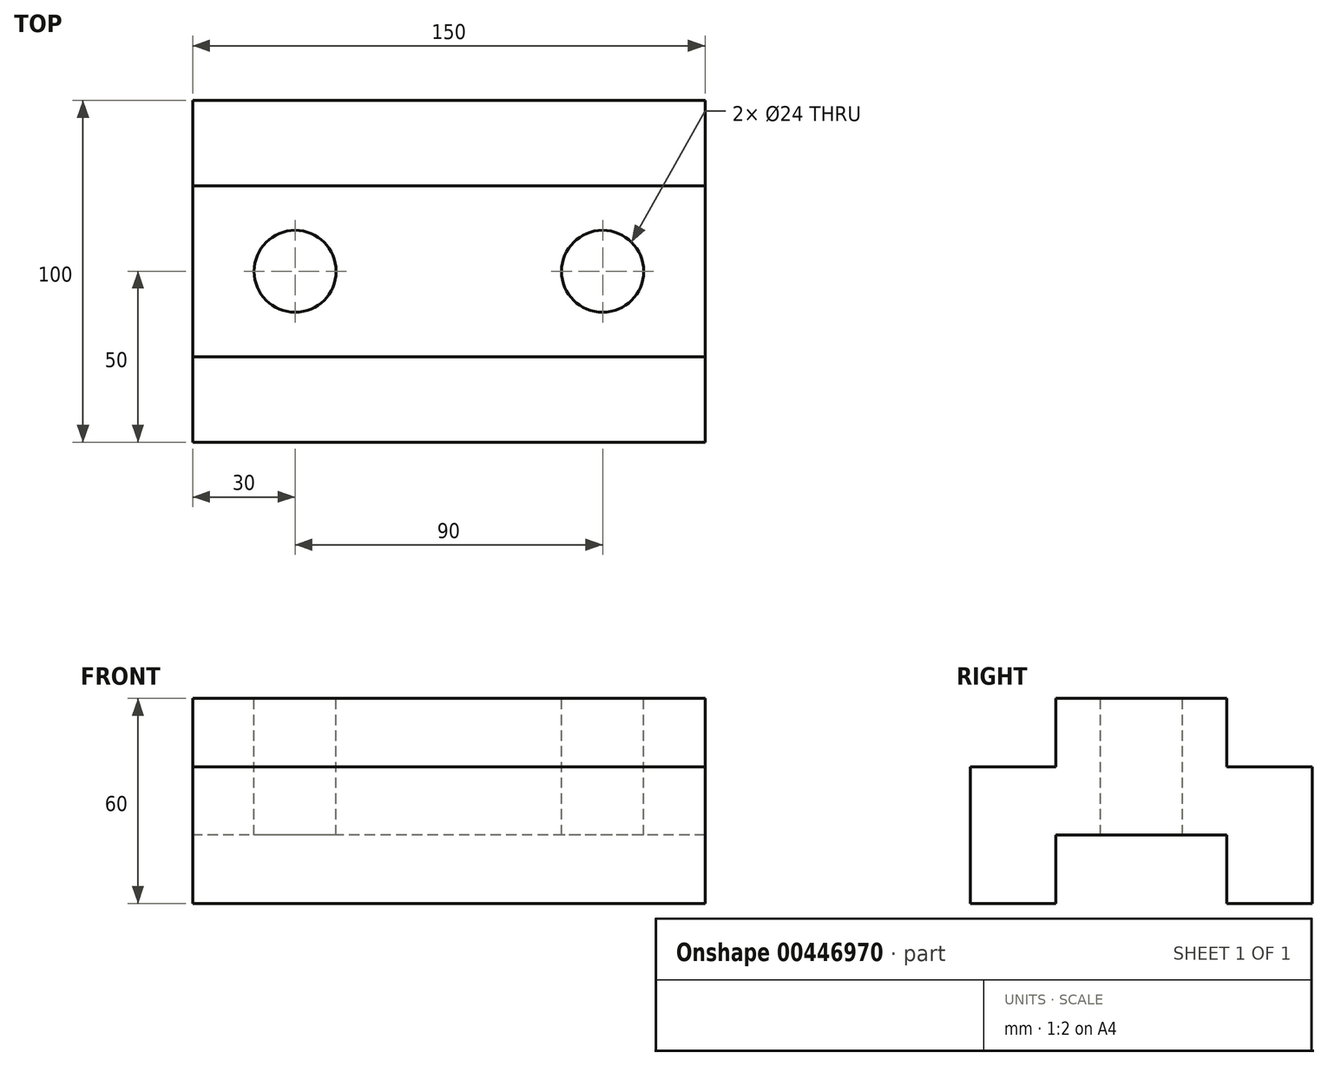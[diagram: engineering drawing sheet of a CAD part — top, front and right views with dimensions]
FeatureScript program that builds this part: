
annotation { "Feature Type Name" : "Feature", "Feature Type Description" : "" }
export const myFeature = defineFeature(function(context is Context, id is Id, definition is map)
    precondition{}
    {
        {
            var Q0;
            Q0=qCreatedBy(makeId("Right.planeOp"),FACE);
            var sketch = newSketch(context, id + "F0", { "sketchPlane" : qUnion([Q0])});
            skLineSegment(sketch, "E0", {"start": v(0, 0) * mm, "end": v(0, 73.04) * mm, "construction": true});
            skLineSegment(sketch, "E1", {"start": v(0, 60) * mm, "end": v(25, 60) * mm});
            skLineSegment(sketch, "E2", {"start": v(25, 60) * mm, "end": v(25, 40) * mm});
            skLineSegment(sketch, "E3", {"start": v(25, 40) * mm, "end": v(50, 40) * mm});
            skLineSegment(sketch, "E4", {"start": v(50, 40) * mm, "end": v(50, 0) * mm});
            skLineSegment(sketch, "E5", {"start": v(50, 0) * mm, "end": v(25, 0) * mm});
            skLineSegment(sketch, "E6", {"start": v(25, 0) * mm, "end": v(25, 20) * mm});
            skLineSegment(sketch, "E7", {"start": v(25, 20) * mm, "end": v(0, 20) * mm});
            skLineSegment(sketch, "E8.MirrorCS", {"start": v(0, 60) * mm, "end": v(-25, 60) * mm});
            skLineSegment(sketch, "E9.MirrorCS", {"start": v(-25, 60) * mm, "end": v(-25, 40) * mm});
            skLineSegment(sketch, "E10.MirrorCS", {"start": v(-25, 40) * mm, "end": v(-50, 40) * mm});
            skLineSegment(sketch, "E11.MirrorCS", {"start": v(-50, 40) * mm, "end": v(-50, 0) * mm});
            skLineSegment(sketch, "E12.MirrorCS", {"start": v(-50, 0) * mm, "end": v(-25, 0) * mm});
            skLineSegment(sketch, "E13.MirrorCS", {"start": v(-25, 0) * mm, "end": v(-25, 20) * mm});
            skLineSegment(sketch, "E14.MirrorCS", {"start": v(-25, 20) * mm, "end": v(0, 20) * mm});
            skSolve(sketch);
        }
        {
            var Q0;
            Q0 = qSketchRegion(id + "F0", true);
            extrude(context, id + "F1", {"entities" : qUnion([Q0]), "endBound" : BoundingType.SYMMETRIC, "depth" : 150 * mm});
        }
        {
            var Q0;
            Q0=makeQuery(id+"F1.opExtrude","SWEPT_FACE",FACE,{"disambiguationData":[OSD([sQuery(id+"F0.wireOp",EDGE,"E1"),sQuery(id+"F0.wireOp",EDGE,"E8.MirrorCS")])]});
            var sketch = newSketch(context, id + "F2", { "sketchPlane" : qUnion([Q0])});
            skLineSegment(sketch, "E15", {"start": v(-75, 0) * mm, "end": v(75, 0) * mm, "construction": true});
            skLineSegment(sketch, "E16", {"start": v(0, 25) * mm, "end": v(0, -25) * mm, "construction": true});
            skCircle(sketch, "E17", {"center": v(-45, 0) * mm, "radius": 12 * mm});
            skCircle(sketch, "E18.MirrorC", {"center": v(45, 0) * mm, "radius": 12 * mm});
            skSolve(sketch);
        }
        {
            var Q0;
            Q0 = qSketchRegion(id + "F2", true);
            extrude(context, id + "F3", {"entities" : qUnion([Q0]), "operationType" : NewBodyOperationType.REMOVE, "endBound" : BoundingType.THROUGH_ALL, "oppositeDirection" : true, "depth" : 25 * mm});
        }
    });
